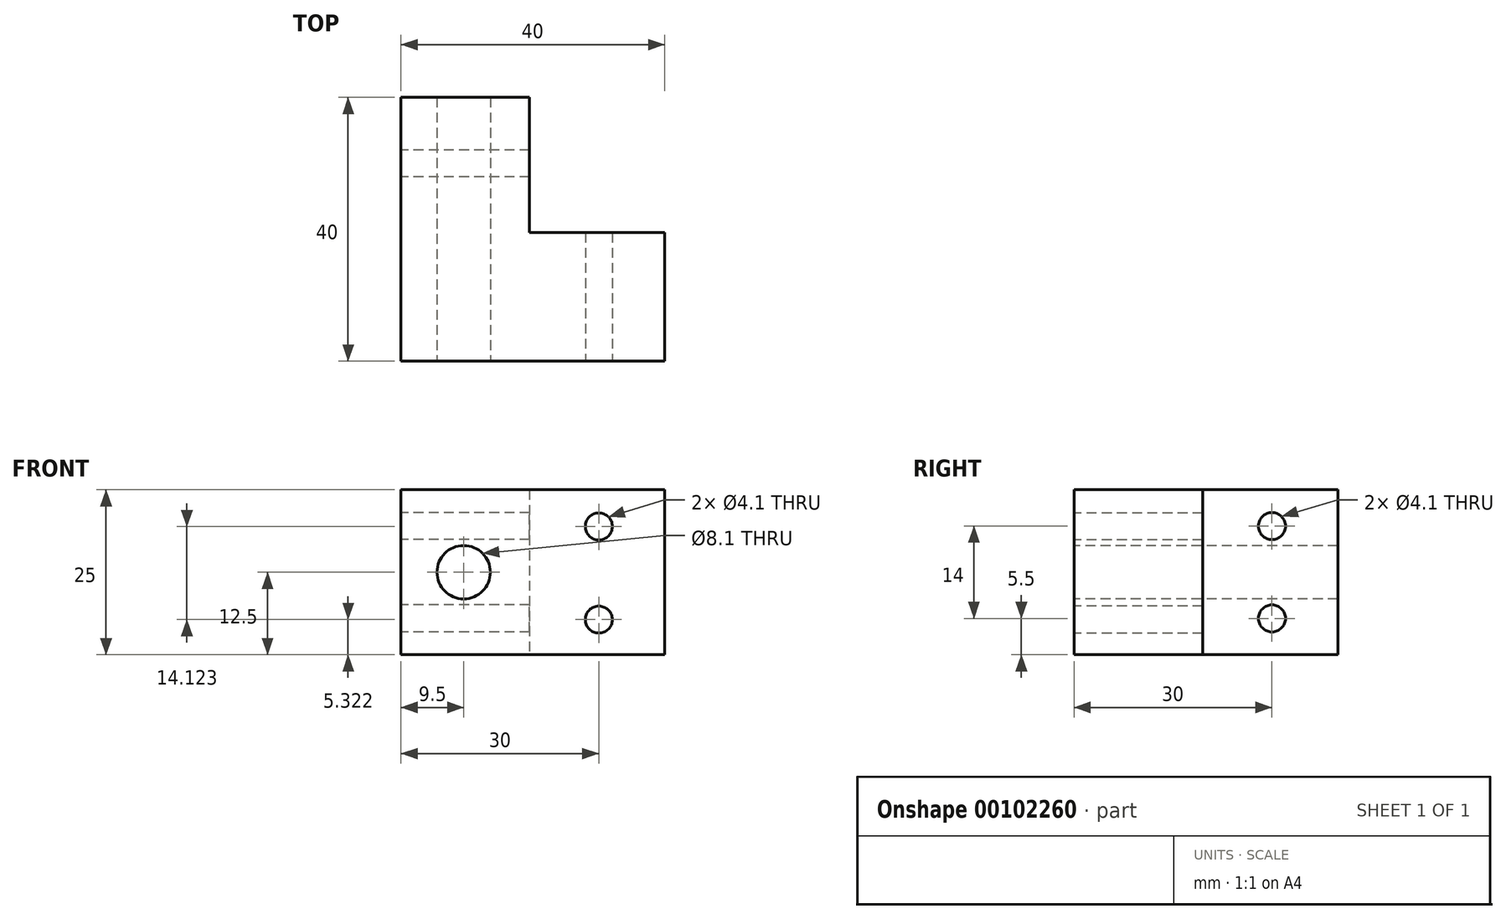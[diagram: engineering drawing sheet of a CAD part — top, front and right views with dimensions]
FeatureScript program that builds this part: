
annotation { "Feature Type Name" : "Feature", "Feature Type Description" : "" }
export const myFeature = defineFeature(function(context is Context, id is Id, definition is map)
    precondition{}
    {
        {
            var Q0;
            Q0=qCreatedBy(makeId("Top.planeOp"),FACE);
            var sketch = newSketch(context, id + "F0", { "sketchPlane" : qUnion([Q0])});
            skLineSegment(sketch, "E0.bottom", {"start": v(-19.5, 20.5) * mm, "end": v(0, 20.5) * mm});
            skLineSegment(sketch, "E0.top", {"start": v(-19.5, -19.5) * mm, "end": v(20.5, -19.5) * mm});
            skLineSegment(sketch, "E0.left", {"start": v(-19.5, 20.5) * mm, "end": v(-19.5, -19.5) * mm});
            skLineSegment(sketch, "E0.right", {"start": v(20.5, 0) * mm, "end": v(20.5, -19.5) * mm});
            skLineSegment(sketch, "E1.top", {"start": v(20.5, 0) * mm, "end": v(0, 0) * mm});
            skLineSegment(sketch, "E1.right", {"start": v(0, 20.5) * mm, "end": v(0, 0) * mm});
            skSolve(sketch);
        }
        {
            var Q0;
            Q0 = qSketchRegion(id + "F0", true);
            extrude(context, id + "F1", {"entities" : qUnion([Q0]), "depth" : 25 * mm});
        }
        {
            var Q0;
            Q0=makeQuery(id+"F1.opExtrude","SWEPT_FACE",FACE,{"disambiguationData":[OSD([sQuery(id+"F0.wireOp",EDGE,"E0.top")])]});
            var sketch = newSketch(context, id + "F2", { "sketchPlane" : qUnion([Q0])});
            skCircle(sketch, "E2", {"center": v(10.5, 19.45) * mm, "radius": 2.05 * mm});
            skCircle(sketch, "E3", {"center": v(10.5, 5.32) * mm, "radius": 2.05 * mm});
            skCircle(sketch, "E4", {"center": v(-10, 12.5) * mm, "radius": 4.05 * mm});
            skSolve(sketch);
        }
        {
            var Q0;
            Q0 = qSketchRegion(id + "F2", true);
            extrude(context, id + "F3", {"entities" : qUnion([Q0]), "operationType" : NewBodyOperationType.REMOVE, "oppositeDirection" : true, "depth" : 45 * mm});
        }
        {
            var Q0;
            Q0=makeQuery(id+"F1.opExtrude","SWEPT_FACE",FACE,{"disambiguationData":[OSD([sQuery(id+"F0.wireOp",EDGE,"E0.left")])]});
            var sketch = newSketch(context, id + "F4", { "sketchPlane" : qUnion([Q0])});
            skCircle(sketch, "E5", {"center": v(-10.5, 19.5) * mm, "radius": 2.05 * mm});
            skCircle(sketch, "E6", {"center": v(-10.5, 5.5) * mm, "radius": 2.05 * mm});
            skSolve(sketch);
        }
        {
            var Q0;
            Q0 = qSketchRegion(id + "F4", true);
            extrude(context, id + "F5", {"entities" : qUnion([Q0]), "operationType" : NewBodyOperationType.REMOVE, "oppositeDirection" : true, "depth" : 25 * mm});
        }
    });
